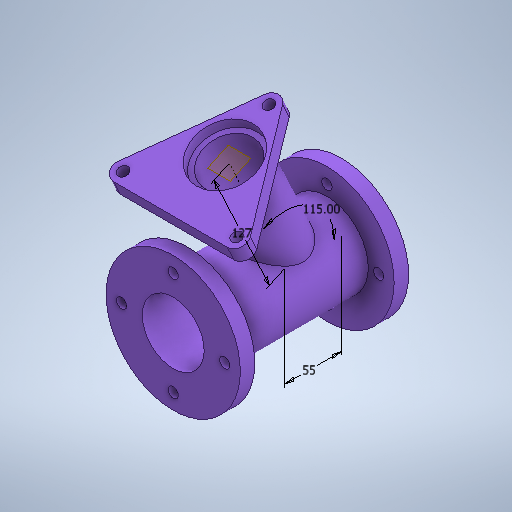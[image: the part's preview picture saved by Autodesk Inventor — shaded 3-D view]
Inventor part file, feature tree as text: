
AUTODESK INVENTOR PART (.ipt)
format: ipt  version: 2025.2 (Build 292293000, 293)  size: 398,336 bytes
history: native  units: in
note: dims shown in document units (in); Inventor stores cm internally (conversion verified against a paired STEP export)
features: sketch x16, extrude x7, plane x4, mirror x1
ambient origin geometry x8: Origin, YZ Plane, XZ Plane, XY Plane, X Axis, Y Axis, Z Axis, Center Point
bodies: Solid1 (feature_tree)
feature tree (28):
  extrude  "Extrusion1"  Depth=2.3622in
  extrude  "Extrusion2"  Depth=5.1181in
  sketch  "Sketch3"  dims[d8=0.3937in d9=1.5748in d11=360.0deg]
  extrude  "Extrusion3"  Depth=0.5512in
  plane  "Work Plane1"
  mirror  "Mirror1"
  plane  "Work Plane2"
  sketch  "Sketch5"  dims[d16=3.7008in d17=0.1718in]
  plane  "Work Plane3"
  sketch  "Sketch6"  dims[d18=5.0in d19=0.7902in]
  sketch  "Sketch7"  dims[d20=2.1654in]
  sketch  "Sketch8"  dims[d21=2.3622in]
  sketch  "Sketch9"  dims[d22=1.9685in]
  sketch  "Sketch10"  dims[d23=0.5512in d24=0.0in]
  sketch  "Sketch11"  dims[d25=0.3937in]
  plane  "Work Plane4"
  extrude  "Extrusion4"  Depth=0.3937in TaperAngle=360.0deg
  extrude  "Extrusion5"  Depth=0.5512in
  extrude  "Extrusion6"  Depth=0.1718in
  extrude  "Extrusion7"  Depth=0.7902in
  sketch  "Sketch1"  dims[d0=3.1496in d1=2.3622in]
  sketch  "Sketch2"  dims[d5=0.5512in d6=0.0in d7=3.937in]
  sketch  "Sketch4"  dims[d13=0.5512in d14=0.0in d15=2.6575in]
  sketch  "Sketch Circular Pattern1"  dims[d2=5.315in d3=0.0in d4=5.1181in]
  sketch  "Sketch12"  dims[d26=4.3307in]
  sketch  "Sketch13"  dims[d28=0.3937in]
  sketch  "Sketch14"  dims[d29=0.3937in]
  sketch  "Sketch15"  dims[d30=0.3937in d31=2.1654in d32=0.3937in d33=0.1969in d34=0.0in d35=0.0in d36=0.3937in d37=0.0in d38=1.9685in d39=4.7244in d40=0.0in]
